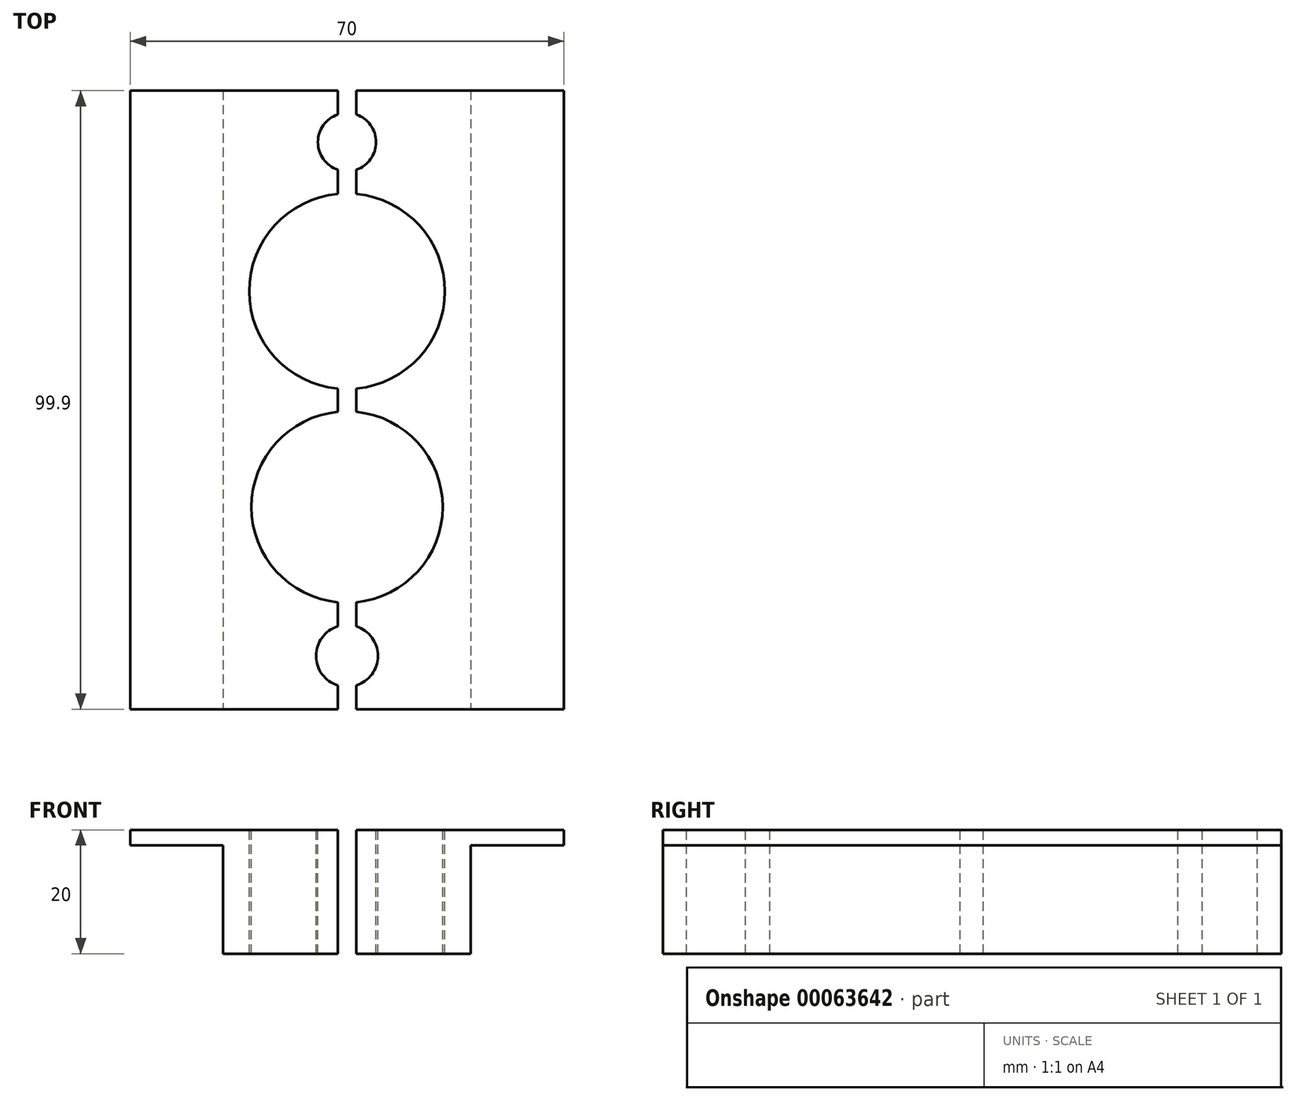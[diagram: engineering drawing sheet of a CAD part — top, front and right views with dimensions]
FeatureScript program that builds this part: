
annotation { "Feature Type Name" : "Feature", "Feature Type Description" : "" }
export const myFeature = defineFeature(function(context is Context, id is Id, definition is map)
    precondition{}
    {
        {
            var Q0;
            Q0=qCreatedBy(makeId("Top.planeOp"),FACE);
            var sketch = newSketch(context, id + "F0", { "sketchPlane" : qUnion([Q0])});
            skLineSegment(sketch, "E0.bottom", {"start": v(-35, 49.95) * mm, "end": v(35, 49.95) * mm});
            skLineSegment(sketch, "E0.top", {"start": v(-35, -49.95) * mm, "end": v(35, -49.95) * mm});
            skLineSegment(sketch, "E0.left", {"start": v(-35, 49.95) * mm, "end": v(-35, -49.95) * mm});
            skLineSegment(sketch, "E0.right", {"start": v(35, 49.95) * mm, "end": v(35, -49.95) * mm});
            skPoint(sketch, "E1", {"position": v(0, 49.95) * mm});
            skPoint(sketch, "E2", {"position": v(35, 0) * mm});
            skCircle(sketch, "E3", {"center": v(0, -41.35) * mm, "radius": 5 * mm});
            skCircle(sketch, "E4", {"center": v(0, -17.3) * mm, "radius": 15.45 * mm});
            skCircle(sketch, "E5", {"center": v(0, 17.55) * mm, "radius": 15.8 * mm});
            skCircle(sketch, "E6", {"center": v(0, 41.65) * mm, "radius": 4.7 * mm});
            skSolve(sketch);
        }
        {
            var Q0;
            Q0=makeQuery(id+"F0.imprint","IMPRINT",FACE,{"disambiguationData":[TD([[makeQuery(id+"F0.imprint","IMPRINT",EDGE,{"derivedFrom":sQuery(id+"F0.wireOp",EDGE,"E0.bottom")}),-1.0]])]});
            extrude(context, id + "F1", {"entities" : qUnion([Q0]), "oppositeDirection" : true, "depth" : 20 * mm});
        }
        {
            var Q0;
            Q0=qCreatedBy(makeId("Front.planeOp"),FACE);
            var sketch = newSketch(context, id + "F2", { "sketchPlane" : qUnion([Q0])});
            skLineSegment(sketch, "E7", {"start": v(0, 0) * mm, "end": v(1.5, 0) * mm});
            skLineSegment(sketch, "E8", {"start": v(1.5, 0) * mm, "end": v(1.5, -5) * mm});
            skLineSegment(sketch, "E9", {"start": v(1.5, -5) * mm, "end": v(1.5, -5) * mm});
            skLineSegment(sketch, "E10", {"start": v(1.5, -5) * mm, "end": v(1.5, -32.9) * mm});
            skLineSegment(sketch, "E11", {"start": v(1.5, -32.9) * mm, "end": v(0, -32.9) * mm});
            skLineSegment(sketch, "E12", {"start": v(0, -32.9) * mm, "end": v(0, 0) * mm});
            skLineSegment(sketch, "E13", {"start": v(20, -33.1) * mm, "end": v(20, -2.5) * mm});
            skLineSegment(sketch, "E14", {"start": v(20, -2.5) * mm, "end": v(42.18, -2.5) * mm});
            skLineSegment(sketch, "E15", {"start": v(42.18, -2.5) * mm, "end": v(42.18, -33.1) * mm});
            skLineSegment(sketch, "E16", {"start": v(42.18, -33.1) * mm, "end": v(20, -33.1) * mm});
            skLineSegment(sketch, "E17.MirrorCS", {"start": v(-1.5, -32.9) * mm, "end": v(0, -32.9) * mm});
            skLineSegment(sketch, "E18.MirrorCS", {"start": v(-1.5, -5) * mm, "end": v(-1.5, -5) * mm});
            skLineSegment(sketch, "E19.MirrorCS", {"start": v(0, 0) * mm, "end": v(-1.5, 0) * mm});
            skLineSegment(sketch, "E20.MirrorCS", {"start": v(-1.5, -5) * mm, "end": v(-1.5, -32.9) * mm});
            skLineSegment(sketch, "E21.MirrorCS", {"start": v(-1.5, 0) * mm, "end": v(-1.5, -5) * mm});
            skLineSegment(sketch, "E22.MirrorCS", {"start": v(-42.18, -33.1) * mm, "end": v(-20, -33.1) * mm});
            skLineSegment(sketch, "E23.MirrorCS", {"start": v(-42.18, -2.5) * mm, "end": v(-42.18, -33.1) * mm});
            skLineSegment(sketch, "E24.MirrorCS", {"start": v(-20, -2.5) * mm, "end": v(-42.18, -2.5) * mm});
            skLineSegment(sketch, "E25.MirrorCS", {"start": v(-20, -33.1) * mm, "end": v(-20, -2.5) * mm});
            skSolve(sketch);
        }
        {
            var Q0;
            Q0 = qSketchRegion(id + "F2", true);
            extrude(context, id + "F3", {"entities" : qUnion([Q0]), "operationType" : NewBodyOperationType.REMOVE, "endBound" : BoundingType.THROUGH_ALL, "depth" : 25 * mm, "hasSecondDirection" : true, "secondDirectionBound" : SecondDirectionBoundingType.THROUGH_ALL, "secondDirectionOppositeDirection" : true, "secondDirectionDepth" : 25 * mm});
        }
    });
